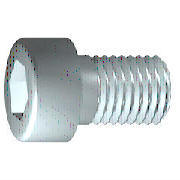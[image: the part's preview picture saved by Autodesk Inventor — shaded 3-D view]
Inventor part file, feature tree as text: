
AUTODESK INVENTOR PART (.ipt)
format: ipt  version: 2019 (Build 230136000, 136)  size: 189,952 bytes
history: native  units: mm (DEFAULTED — no unit token found)
features: sketch x2, extrude x1, plane x1, fillet x1
ambient origin geometry x7: Origin, YZ Plane, XY Plane, X Axis, Y Axis, Z Axis, Center Point
bodies: Solid1 (feature_tree), Body (feature_tree)
feature tree (5):
  extrude  "Slot"  Depth=3.0mm
  plane  "Work Plane1"
  fillet  "Fillet2"  Radius=3.0mm
  sketch  "Sketch1"  dims[d1=14.75mm d2=0.306825mm d3=3.0mm]
  sketch  "Sketch2"  dims[d4=1.3mm d5=60.0deg d6=3.0mm d7=3.0mm d8=2.886751mm d9=5.5mm d10=90.0deg d11=10.0mm d12=0.0mm d13=14.75mm d14=0.0mm d15=0.306725mm d16=0.306725mm d17=0.3mm d19=0.0mm d26=16.0mm d27=45.0deg d28=0.0mm d29=0.0mm d30=0.1mm]
